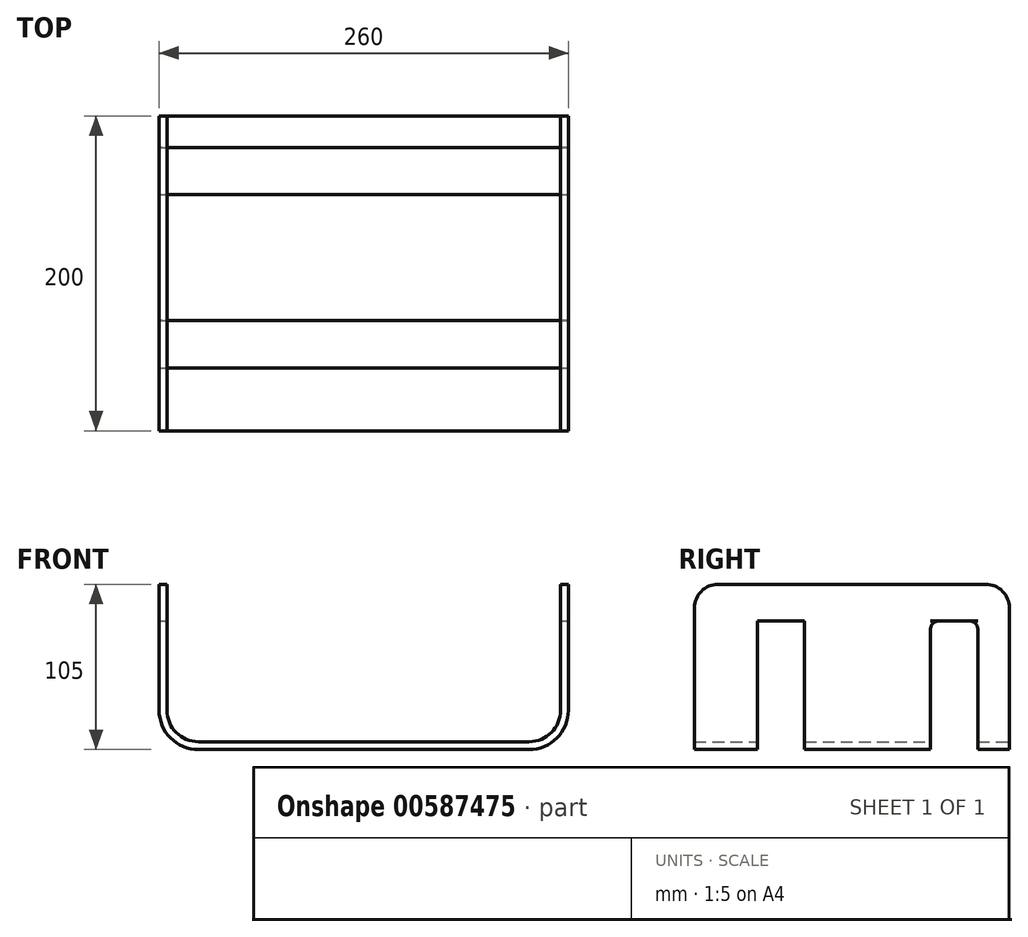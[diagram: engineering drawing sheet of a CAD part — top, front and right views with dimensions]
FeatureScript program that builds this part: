
annotation { "Feature Type Name" : "Feature", "Feature Type Description" : "" }
export const myFeature = defineFeature(function(context is Context, id is Id, definition is map)
    precondition{}
    {
        {
            var Q0;
            Q0=qCreatedBy(makeId("Front.planeOp"),FACE);
            var sketch = newSketch(context, id + "F0", { "sketchPlane" : qUnion([Q0])});
            skLineSegment(sketch, "E0", {"start": v(-127.55, 43.5) * mm, "end": v(-127.55, -36.5) * mm});
            skLineSegment(sketch, "E1", {"start": v(-107.55, -56.5) * mm, "end": v(102.45, -56.5) * mm});
            skLineSegment(sketch, "E2", {"start": v(122.45, -36.5) * mm, "end": v(122.45, 43.5) * mm});
            skPoint(sketch, "E3.visualSharp", {"position": v(-127.55, -56.5) * mm});
            skArc(sketch, "E3.filletArc", {"start": v(-127.55, -36.5) * mm, "mid": v(-121.7, -50.64) * mm, "end": v(-107.55, -56.5) * mm});
            skPoint(sketch, "E4.visualSharp", {"position": v(122.45, -56.5) * mm});
            skArc(sketch, "E4.filletArc", {"start": v(102.45, -56.5) * mm, "mid": v(116.59, -50.64) * mm, "end": v(122.45, -36.5) * mm});
            skLineSegment(sketch, "E5.0", {"start": v(127.45, -36.5) * mm, "end": v(127.45, 43.5) * mm});
            skLineSegment(sketch, "E5.1", {"start": v(-132.55, 43.5) * mm, "end": v(-132.55, -36.5) * mm});
            skArc(sketch, "E5.2", {"start": v(-132.55, -36.5) * mm, "mid": v(-125.23, -54.18) * mm, "end": v(-107.55, -61.5) * mm});
            skLineSegment(sketch, "E5.3", {"start": v(-107.55, -61.5) * mm, "end": v(102.45, -61.5) * mm});
            skArc(sketch, "E5.4", {"start": v(102.45, -61.5) * mm, "mid": v(120.12, -54.18) * mm, "end": v(127.45, -36.5) * mm});
            skLineSegment(sketch, "E6", {"start": v(-132.55, 43.5) * mm, "end": v(-127.55, 43.5) * mm});
            skLineSegment(sketch, "E7", {"start": v(122.45, 43.5) * mm, "end": v(127.45, 43.5) * mm});
            skSolve(sketch);
        }
        {
            var Q0;
            Q0=qCreatedBy(makeId("Right.planeOp"),FACE);
            cPlane(context, id + "F1", {"entities" : qUnion([Q0]), "cplaneType" : CPlaneType.OFFSET, "offset" : 200 * mm, "width" : 150 * mm, "height" : 150 * mm});
        }
        {
            var Q0;
            Q0=makeQuery(id+"F0.imprint","IMPRINT",FACE,{"disambiguationData":[TD([[makeQuery(id+"F0.imprint","IMPRINT",EDGE,{"derivedFrom":sQuery(id+"F0.wireOp",EDGE,"E0")}),-1.0]])]});
            extrude(context, id + "F2", {"entities" : qUnion([Q0]), "depth" : 200 * mm, "offsetDistance" : 25 * mm});
        }
        {
            var Q0;
            Q0=qCreatedBy(id+"F1.planeOp",FACE);
            var sketch = newSketch(context, id + "F3", { "sketchPlane" : qUnion([Q0])});
            skLineSegment(sketch, "E8", {"start": v(-160, 20.09) * mm, "end": v(-160, -79.91) * mm});
            skLineSegment(sketch, "E9", {"start": v(-160, -79.91) * mm, "end": v(-130, -79.91) * mm});
            skLineSegment(sketch, "E10", {"start": v(-20, -79.91) * mm, "end": v(-20, 20.09) * mm});
            skLineSegment(sketch, "E11", {"start": v(-20, 20.09) * mm, "end": v(-50, 20.09) * mm});
            skLineSegment(sketch, "E12", {"start": v(-50, 20.09) * mm, "end": v(-50, -79.91) * mm});
            skLineSegment(sketch, "E13", {"start": v(-130, -79.91) * mm, "end": v(-130, 20.09) * mm});
            skLineSegment(sketch, "E14", {"start": v(-130, 20.09) * mm, "end": v(-160, 20.09) * mm});
            skLineSegment(sketch, "E15.filletArc", {"start": v(-130, -79.91) * mm, "end": v(-130, -79.91) * mm});
            skLineSegment(sketch, "E16", {"start": v(-50, -79.91) * mm, "end": v(-20, -79.91) * mm});
            skLineSegment(sketch, "E17.filletArc", {"start": v(-20, -79.91) * mm, "end": v(-20, -79.91) * mm});
            skSolve(sketch);
        }
        {
            var Q0;
            Q0=makeQuery(id+"F3.imprint","IMPRINT",FACE,{"disambiguationData":[TD([[makeQuery(id+"F3.imprint","IMPRINT",EDGE,{"derivedFrom":sQuery(id+"F3.wireOp",EDGE,"E8")}),1.0]])]});
            var Q1;
            Q1=makeQuery(id+"F3.imprint","IMPRINT",FACE,{"disambiguationData":[TD([[makeQuery(id+"F3.imprint","IMPRINT",EDGE,{"derivedFrom":sQuery(id+"F3.wireOp",EDGE,"E10")}),1.0]])]});
            extrude(context, id + "F4", {"entities" : qUnion([Q0, Q1]), "oppositeDirection" : true, "depth" : 500 * mm, "offsetDistance" : 25 * mm});
        }
        {
            var Q0;
            Q0=makeQuery(id+"F4.opExtrude","SWEPT_BODY",BODY,{"disambiguationData":[OSD([sQuery(id+"F3.wireOp",EDGE,"E8"),sQuery(id+"F3.wireOp",EDGE,"E9"),sQuery(id+"F3.wireOp",EDGE,"E10"),sQuery(id+"F3.wireOp",EDGE,"E11"),sQuery(id+"F3.wireOp",EDGE,"E12"),sQuery(id+"F3.wireOp",EDGE,"sOlcA3gc-G1YB-Knjk-OlmM-VOpdweEhVf90"),sQuery(id+"F3.wireOp",EDGE,"E13"),sQuery(id+"F3.wireOp",EDGE,"E14")])]});
            var Q1;
            Q1=makeQuery(id+"F4.opExtrude","SWEPT_BODY",BODY,{"disambiguationData":[OSD([sQuery(id+"F3.wireOp",EDGE,"E10"),sQuery(id+"F3.wireOp",EDGE,"E11"),sQuery(id+"F3.wireOp",EDGE,"E12"),sQuery(id+"F3.wireOp",EDGE,"E16")])]});
            var Q2;
            Q2=makeQuery(id+"F2.opExtrude","SWEPT_BODY",BODY,{"disambiguationData":[OSD([sQuery(id+"F0.wireOp",EDGE,"E0"),sQuery(id+"F0.wireOp",EDGE,"E1"),sQuery(id+"F0.wireOp",EDGE,"E2"),sQuery(id+"F0.wireOp",EDGE,"E3.filletArc"),sQuery(id+"F0.wireOp",EDGE,"E4.filletArc"),sQuery(id+"F0.wireOp",EDGE,"E5.0"),sQuery(id+"F0.wireOp",EDGE,"E5.1"),sQuery(id+"F0.wireOp",EDGE,"E5.2"),sQuery(id+"F0.wireOp",EDGE,"E5.3"),sQuery(id+"F0.wireOp",EDGE,"E5.4"),sQuery(id+"F0.wireOp",EDGE,"E6"),sQuery(id+"F0.wireOp",EDGE,"E7")])]});
            booleanBodies(context, id + "F5", {"operationType" : BooleanOperationType.SUBTRACTION, "tools" : qUnion([Q0, Q1]), "targets" : qUnion([Q2])});
        }
        {
            var Q0;
            Q0=makeQuery(id+"F2.opExtrude","CAP_EDGE",EDGE,{"disambiguationData":[OSD([sQuery(id+"F0.wireOp",EDGE,"E6")])],"isStart":false});
            var Q1;
            Q1=makeQuery(id+"F2.opExtrude","CAP_EDGE",EDGE,{"disambiguationData":[OSD([sQuery(id+"F0.wireOp",EDGE,"E6")])],"isStart":true});
            var Q2;
            Q2=makeQuery(id+"F2.opExtrude","CAP_EDGE",EDGE,{"disambiguationData":[OSD([sQuery(id+"F0.wireOp",EDGE,"E7")])],"isStart":false});
            var Q3;
            Q3=makeQuery(id+"F2.opExtrude","CAP_EDGE",EDGE,{"disambiguationData":[OSD([sQuery(id+"F0.wireOp",EDGE,"E7")])],"isStart":true});
            fillet(context, id + "F6", {"entities" : qUnion([Q0, Q1, Q2, Q3]), "radius" : 15 * mm, "tangentPropagation" : true, "allowEdgeOverflow" : false});
        }
        {
            var Q0;
            {var subQ0=sQuery(id+"F3.wireOp",EDGE,"E10");var subQ1=sQuery(id+"F3.wireOp",EDGE,"E11");Q0=makeQuery(id+"F5.opBoolean","COPY",EDGE,{"disambiguationData":[TD([makeQuery(id+"F2.opExtrude","SWEPT_FACE",FACE,{"disambiguationData":[OSD([sQuery(id+"F0.wireOp",EDGE,"E2")])]})])],"derivedFrom":makeQuery(id+"F4.opExtrude","SWEPT_EDGE",EDGE,{"disambiguationData":[OSD([subQ0,subQ1])]})});}
            var Q1;
            {var subQ0=sQuery(id+"F3.wireOp",EDGE,"E11");var subQ1=sQuery(id+"F3.wireOp",EDGE,"E12");Q1=makeQuery(id+"F5.opBoolean","COPY",EDGE,{"disambiguationData":[TD([makeQuery(id+"F2.opExtrude","SWEPT_FACE",FACE,{"disambiguationData":[OSD([sQuery(id+"F0.wireOp",EDGE,"E2")])]})])],"derivedFrom":makeQuery(id+"F4.opExtrude","SWEPT_EDGE",EDGE,{"disambiguationData":[OSD([subQ0,subQ1])]})});}
            fillet(context, id + "F7", {"entities" : qUnion([Q0, Q1]), "radius" : 5 * mm, "tangentPropagation" : true, "allowEdgeOverflow" : false});
        }
    });
